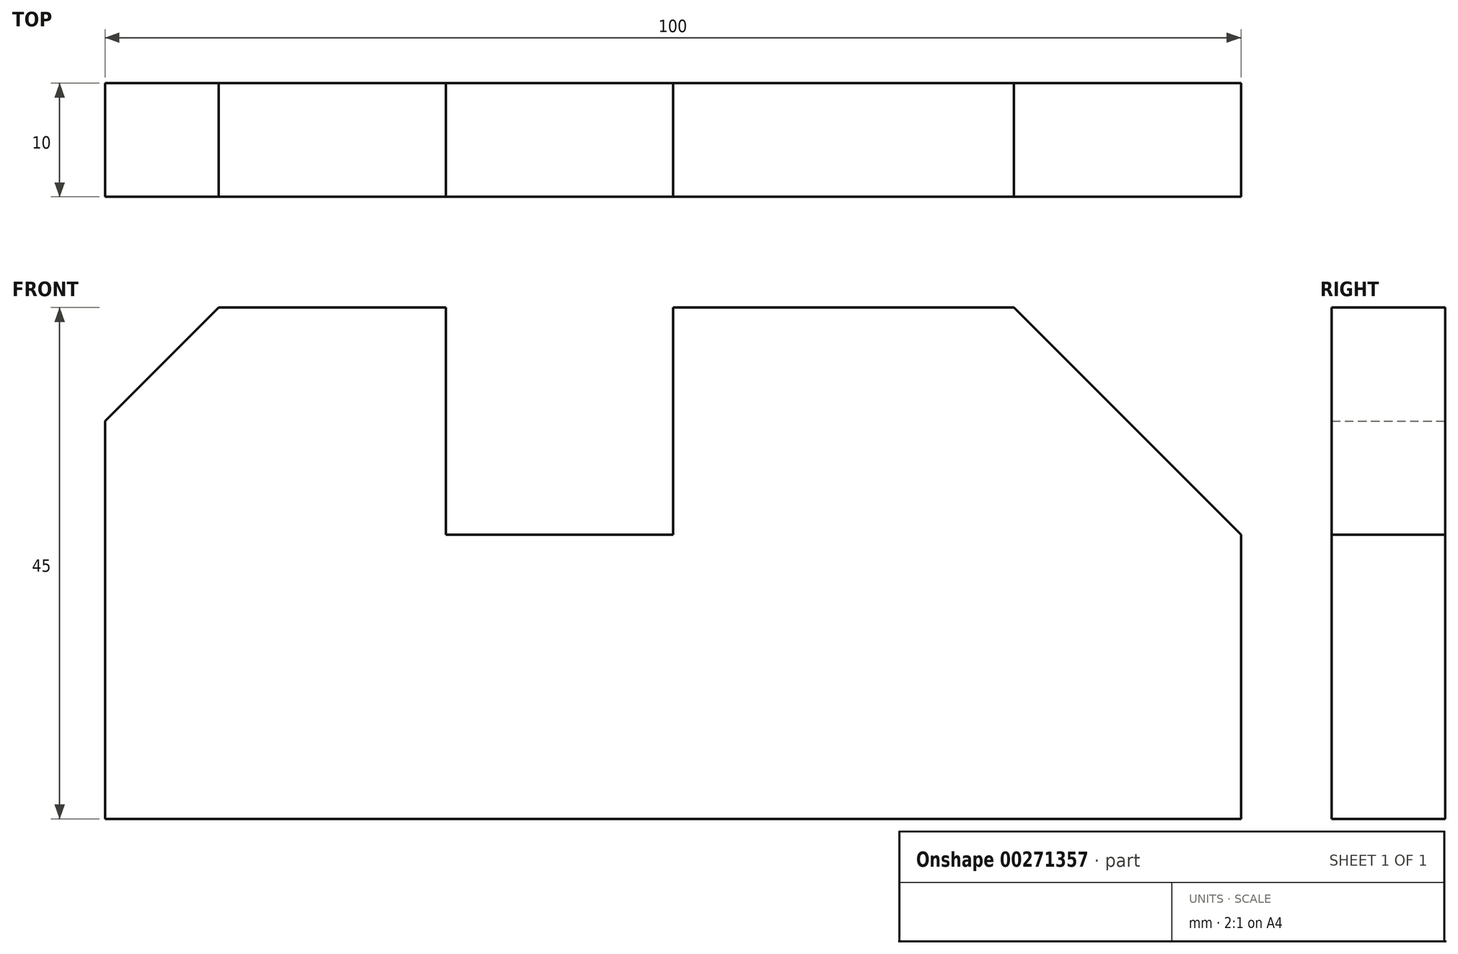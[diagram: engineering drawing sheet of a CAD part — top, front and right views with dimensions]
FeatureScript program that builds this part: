
annotation { "Feature Type Name" : "Feature", "Feature Type Description" : "" }
export const myFeature = defineFeature(function(context is Context, id is Id, definition is map)
    precondition{}
    {
        {
            var Q0;
            Q0=qCreatedBy(makeId("Front.planeOp"),FACE);
            var sketch = newSketch(context, id + "F0", { "sketchPlane" : qUnion([Q0])});
            skLineSegment(sketch, "E0", {"start": v(0, 0) * mm, "end": v(100, 0) * mm});
            skPoint(sketch, "E1", {"position": v(10, 45) * mm});
            skLineSegment(sketch, "E2", {"start": v(10, 45) * mm, "end": v(0, 35) * mm});
            skLineSegment(sketch, "E3", {"start": v(0, 35) * mm, "end": v(0, 0) * mm});
            skLineSegment(sketch, "E4", {"start": v(10, 45) * mm, "end": v(30, 45) * mm});
            skLineSegment(sketch, "E5", {"start": v(30, 45) * mm, "end": v(30, 25) * mm});
            skLineSegment(sketch, "E6", {"start": v(30, 25) * mm, "end": v(50, 25) * mm});
            skLineSegment(sketch, "E7", {"start": v(50, 25) * mm, "end": v(50, 45) * mm});
            skLineSegment(sketch, "E8", {"start": v(50, 45) * mm, "end": v(80, 45) * mm});
            skLineSegment(sketch, "E9", {"start": v(80, 45) * mm, "end": v(100, 25) * mm});
            skLineSegment(sketch, "E10", {"start": v(100, 25) * mm, "end": v(100, 0) * mm});
            skSolve(sketch);
        }
        {
            var Q0;
            Q0 = qSketchRegion(id + "F0", true);
            extrude(context, id + "F1", {"entities" : qUnion([Q0]), "depth" : 10 * mm});
        }
    });
